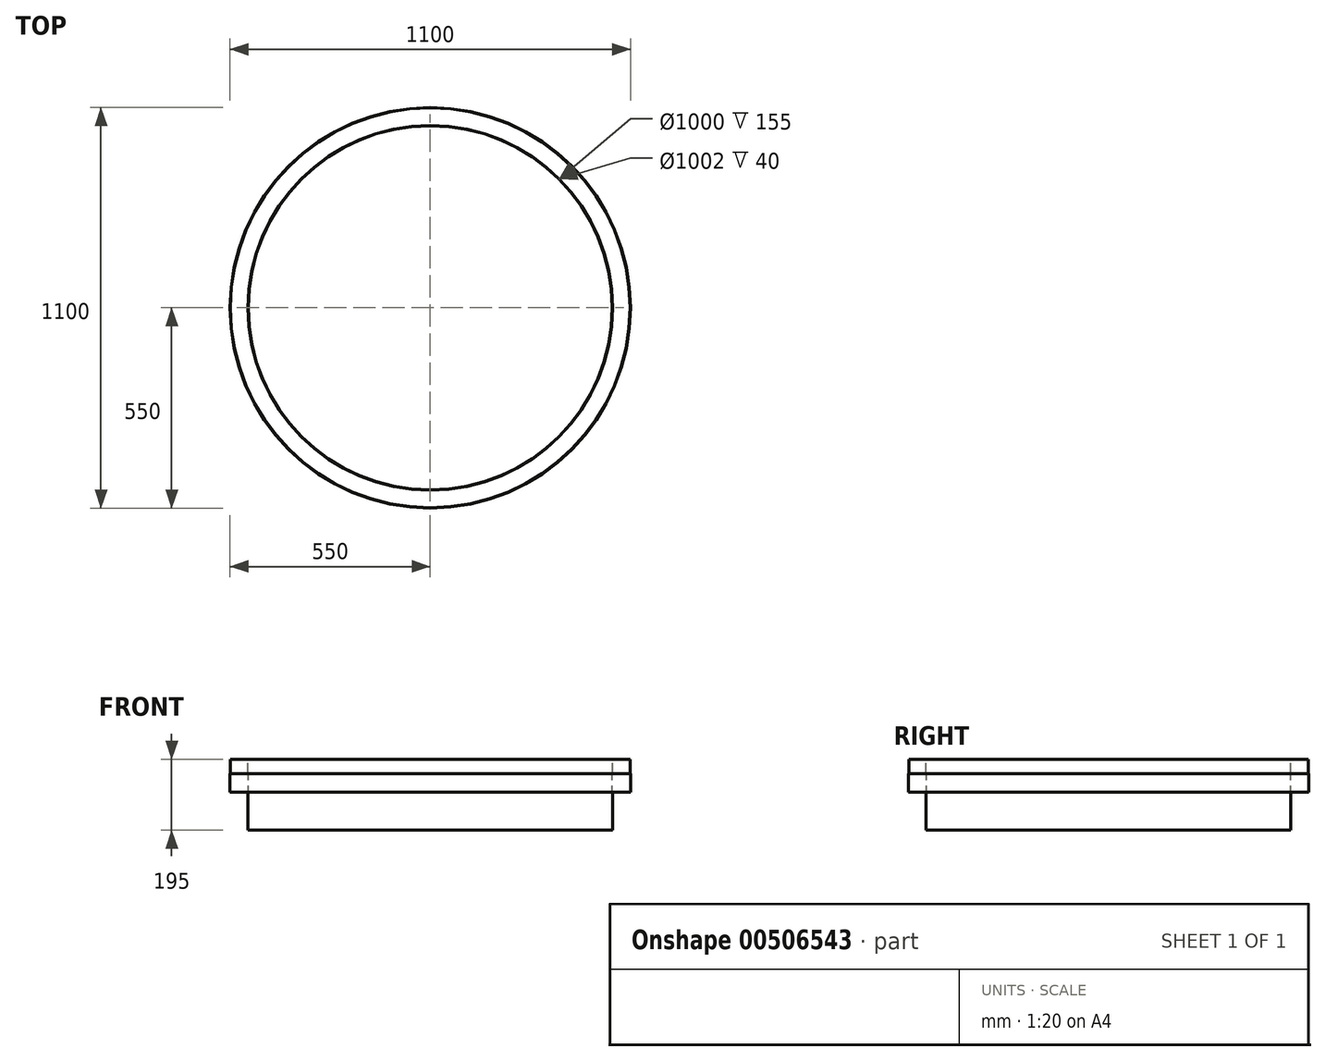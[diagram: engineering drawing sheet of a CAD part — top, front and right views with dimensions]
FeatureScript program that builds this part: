
annotation { "Feature Type Name" : "Feature", "Feature Type Description" : "" }
export const myFeature = defineFeature(function(context is Context, id is Id, definition is map)
    precondition{}
    {
        {
            var Q0;
            Q0=qCreatedBy(makeId("Front.planeOp"),FACE);
            var sketch = newSketch(context, id + "F0", { "sketchPlane" : qUnion([Q0])});
            skLineSegment(sketch, "E0", {"start": v(0, 710.75) * mm, "end": v(0, -704.58) * mm, "construction": true});
            skLineSegment(sketch, "E1", {"start": v(-500, 295.65) * mm, "end": v(-500, 410.65) * mm});
            skLineSegment(sketch, "E2", {"start": v(-500, 410.65) * mm, "end": v(-501, 410.65) * mm});
            skLineSegment(sketch, "E3", {"start": v(-549, 410.65) * mm, "end": v(-550, 410.65) * mm});
            skLineSegment(sketch, "E4", {"start": v(-550, 410.65) * mm, "end": v(-550, 360.65) * mm});
            skLineSegment(sketch, "E5", {"start": v(-550, 360.65) * mm, "end": v(-501, 360.65) * mm});
            skLineSegment(sketch, "E6", {"start": v(-501, 360.65) * mm, "end": v(-501, 295.65) * mm});
            skLineSegment(sketch, "E7", {"start": v(-549, 450.65) * mm, "end": v(-549, 410.65) * mm});
            skLineSegment(sketch, "E8", {"start": v(-549, 450.65) * mm, "end": v(-501, 450.65) * mm});
            skLineSegment(sketch, "E9", {"start": v(-501, 410.65) * mm, "end": v(-501, 450.65) * mm});
            skLineSegment(sketch, "E10", {"start": v(-500, 295.65) * mm, "end": v(-500, 255.65) * mm});
            skLineSegment(sketch, "E11", {"start": v(-501, 295.65) * mm, "end": v(-501, 255.65) * mm});
            skLineSegment(sketch, "E12", {"start": v(-501, 255.65) * mm, "end": v(-500, 255.65) * mm});
            skSolve(sketch);
        }
        {
            var Q0;
            Q0=qSketchRegion(id+"F0",true);
            var Q1;
            Q1=sQuery(id+"F0.wireOp",EDGE,"E0");
            revolve(context, id + "F1", {"entities" : qUnion([Q0]), "axis" : qUnion([Q1]), "revolveType" : RevolveType.FULL});
        }
    });
